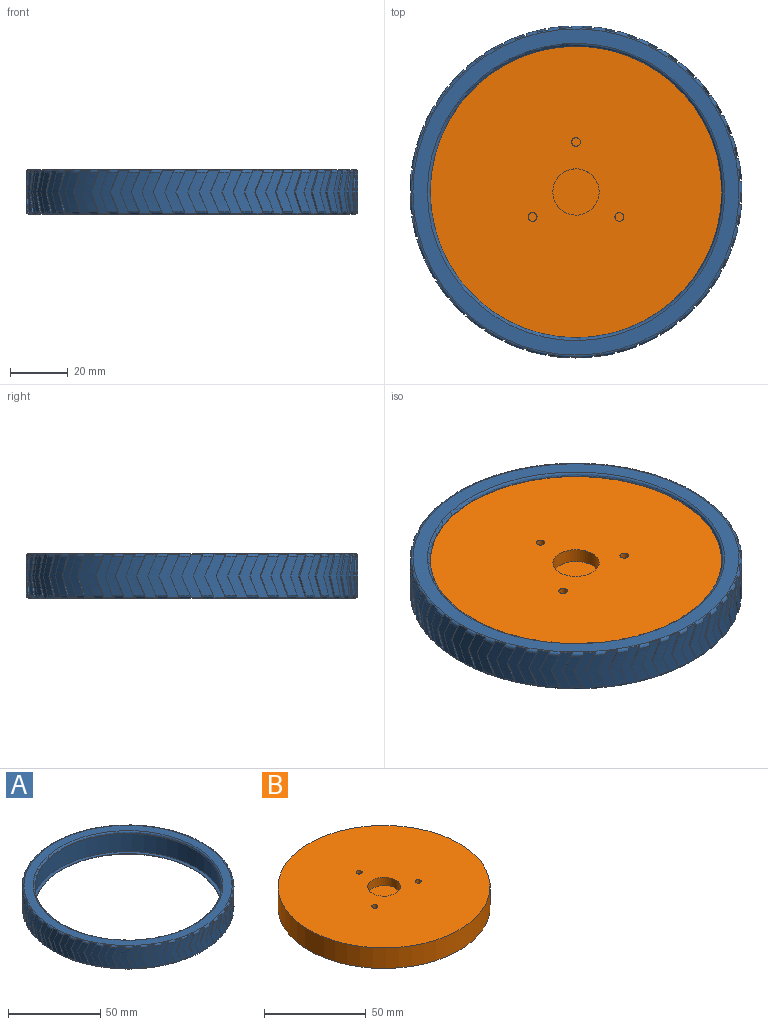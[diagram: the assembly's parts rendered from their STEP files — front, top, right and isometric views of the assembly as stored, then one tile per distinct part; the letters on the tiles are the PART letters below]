
ASSEMBLY  parts=2 mates=1
PART A: 280 faces, bbox 124.3x124.3x15.4 mm
  f0: cylinder r=57.4mm len=13.35mm, axis (0,0,1), area 53.5mm2, adj f45,f46,f272,f273,f275,f276
  f1: cylinder r=57.4mm len=13.35mm, axis (0,0,1), area 53.5mm2, adj f45,f46,f60,f61,f277,f278
  f2: cylinder r=57.4mm len=13.35mm, axis (0,0,1), area 53.5mm2, adj f45,f46,f267,f268,f270,f271
  f3: cylinder r=57.4mm len=13.35mm, axis (0,0,1), area 53.5mm2, adj f45,f46,f262,f263,f265,f266
  f4: cylinder r=57.4mm len=13.35mm, axis (0,0,1), area 53.5mm2, adj f45,f46,f257,f258,f260,f261
  f5: cylinder r=57.4mm len=13.35mm, axis (0,0,1), area 53.5mm2, adj f45,f46,f252,f253,f255,f256
  f6: cylinder r=57.4mm len=13.35mm, axis (0,0,1), area 53.5mm2, adj f45,f46,f247,f248,f250,f251
  f7: cylinder r=57.4mm len=13.35mm, axis (0,0,1), area 53.5mm2, adj f45,f46,f242,f243,f245,f246
  f8: cylinder r=57.4mm len=13.35mm, axis (0,0,1), area 53.5mm2, adj f45,f46,f237,f238,f240,f241
  f9: cylinder r=57.4mm len=13.35mm, axis (0,0,1), area 53.5mm2, adj f45,f46,f232,f233,f235,f236
  f10: cylinder r=57.4mm len=13.35mm, axis (0,0,1), area 53.5mm2, adj f45,f46,f227,f228,f230,f231
  f11: cylinder r=57.4mm len=13.35mm, axis (0,0,1), area 53.5mm2, adj f45,f46,f222,f223,f225,f226
  f12: cylinder r=57.4mm len=13.35mm, axis (0,0,1), area 53.5mm2, adj f45,f46,f217,f218,f220,f221
  f13: cylinder r=57.4mm len=13.35mm, axis (0,0,1), area 53.5mm2, adj f45,f46,f212,f213,f215,f216
  f14: cylinder r=57.4mm len=13.35mm, axis (0,0,1), area 53.5mm2, adj f45,f46,f207,f208,f210,f211
  f15: cylinder r=57.4mm len=13.35mm, axis (0,0,1), area 53.5mm2, adj f45,f46,f202,f203,f205,f206
  f16: cylinder r=57.4mm len=13.35mm, axis (0,0,1), area 53.5mm2, adj f45,f46,f197,f198,f200,f201
  f17: cylinder r=57.4mm len=13.35mm, axis (0,0,1), area 53.5mm2, adj f45,f46,f192,f193,f195,f196
  f18: cylinder r=57.4mm len=13.35mm, axis (0,0,1), area 53.5mm2, adj f45,f46,f187,f188,f190,f191
  f19: cylinder r=57.4mm len=13.35mm, axis (0,0,1), area 53.5mm2, adj f45,f46,f182,f183,f185,f186
  f20: cylinder r=57.4mm len=13.35mm, axis (0,0,1), area 53.5mm2, adj f45,f46,f177,f178,f180,f181
  f21: cylinder r=57.4mm len=13.35mm, axis (0,0,1), area 53.5mm2, adj f45,f46,f172,f173,f175,f176
  f22: cylinder r=57.4mm len=13.35mm, axis (0,0,1), area 53.5mm2, adj f45,f46,f167,f168,f170,f171
  f23: cylinder r=57.4mm len=13.35mm, axis (0,0,1), area 53.5mm2, adj f45,f46,f162,f163,f165,f166
  f24: cylinder r=57.4mm len=13.35mm, axis (0,0,1), area 53.5mm2, adj f45,f46,f157,f158,f160,f161
  f25: cylinder r=57.4mm len=13.35mm, axis (0,0,1), area 53.5mm2, adj f45,f46,f152,f153,f155,f156
  f26: cylinder r=57.4mm len=13.35mm, axis (0,0,1), area 53.5mm2, adj f45,f46,f147,f148,f150,f151
  f27: cylinder r=57.4mm len=13.35mm, axis (0,0,1), area 53.5mm2, adj f45,f46,f142,f143,f145,f146
  f28: cylinder r=57.4mm len=13.35mm, axis (0,0,1), area 53.5mm2, adj f45,f46,f137,f138,f140,f141
  f29: cylinder r=57.4mm len=13.35mm, axis (0,0,1), area 53.5mm2, adj f45,f46,f132,f133,f135,f136
  f30: cylinder r=57.4mm len=13.35mm, axis (0,0,1), area 53.5mm2, adj f45,f46,f127,f128,f130,f131
  f31: cylinder r=57.4mm len=13.35mm, axis (0,0,1), area 53.5mm2, adj f45,f46,f122,f123,f125,f126
  f32: cylinder r=57.4mm len=13.35mm, axis (0,0,1), area 53.5mm2, adj f45,f46,f57,f58,f120,f121
  f33: cylinder r=57.4mm len=13.35mm, axis (0,0,1), area 53.5mm2, adj f45,f46,f112,f113,f115,f116
  f34: cylinder r=57.4mm len=13.35mm, axis (0,0,1), area 53.5mm2, adj f45,f46,f55,f56,f117,f118
  f35: cylinder r=57.4mm len=13.35mm, axis (0,0,1), area 53.5mm2, adj f45,f46,f107,f108,f110,f111
  f36: cylinder r=57.4mm len=13.35mm, axis (0,0,1), area 53.5mm2, adj f45,f46,f102,f103,f105,f106
  f37: cylinder r=57.4mm len=13.35mm, axis (0,0,1), area 53.5mm2, adj f45,f46,f97,f98,f100,f101
  f38: cylinder r=57.4mm len=13.35mm, axis (0,0,1), area 53.5mm2, adj f45,f46,f92,f93,f95,f96
  f39: cylinder r=57.4mm len=13.35mm, axis (0,0,1), area 53.5mm2, adj f45,f46,f87,f88,f90,f91
  f40: cylinder r=57.4mm len=13.35mm, axis (0,0,1), area 53.5mm2, adj f45,f46,f82,f83,f85,f86
  f41: cylinder r=57.4mm len=13.35mm, axis (0,0,1), area 53.5mm2, adj f45,f46,f77,f78,f80,f81
  f42: cylinder r=57.4mm len=13.35mm, axis (0,0,1), area 53.5mm2, adj f45,f46,f72,f73,f75,f76
  f43: cylinder r=57.4mm len=13.35mm, axis (0,0,1), area 53.5mm2, adj f45,f46,f67,f68,f70,f71
  f44: cylinder r=57.4mm len=13.35mm, axis (0,0,1), area 53.5mm2, adj f45,f46,f62,f63,f65,f66
  f45: torus R=56.4mm, axis (0,0,-1), area 356.7mm2, adj f0,f1,f2,f3,f4,f5,f6,f7
  f46: torus R=56.4mm, axis (0,0,-1), area 356.7mm2, adj f0,f1,f2,f3,f4,f5,f6,f7
  f47: plane 104.8x104.8mm, normal (0,0,1), area 645.9mm2, adj f48,f54
  f48: cylinder r=52.4mm len=104.8mm, axis (0,0,1), area 4197.8mm2, adj f47,f49
  f49: cone r=52.4mm half-angle=73.3deg, axis (0,0,-1), area 674.4mm2, adj f48,f50
  f50: cylinder r=50.4mm len=100.8mm, axis (0,0,1), area 63.3mm2, adj f49,f53
  f51: plane 112.8x112.8mm, normal (0,0,1), area 1693.3mm2, adj f45,f53
  f52: plane 112.8x112.8mm, normal (0,0,-1), area 1699.8mm2, adj f46,f54
  f53: torus R=51.4mm, axis (0,0,-1), area 501mm2, adj f50,f51
  f54: torus R=51.38mm, axis (0,0,-1), area 437.1mm2, adj f47,f52
  f55: plane 7.58x3.24mm, normal (-0.92,0,-0.39), area 4.7mm2, adj f34,f46,f56,f59
  f56: plane 7.58x3.24mm, normal (-0.92,0,0.39), area 4.7mm2, adj f34,f45,f55,f59
  f57: plane 7.58x3.24mm, normal (0.92,0,-0.39), area 3.6mm2, adj f32,f45,f58,f59
  f58: plane 7.58x3.24mm, normal (0.92,0,0.39), area 3.6mm2, adj f32,f46,f57,f59
  f59: plane 15.18x7.24mm, normal (0,-1,0), area 60.7mm2, adj f45,f46,f55,f56,f57,f58
  f60: plane 7.58x3.22mm, normal (0.1,-0.91,-0.39), area 4.7mm2, adj f1,f46,f61,f64
  f61: plane 7.58x3.22mm, normal (0.1,-0.91,0.39), area 4.7mm2, adj f1,f45,f60,f64
  f62: plane 7.58x3.22mm, normal (-0.1,0.91,-0.39), area 3.6mm2, adj f44,f45,f63,f64
  f63: plane 7.58x3.22mm, normal (-0.1,0.91,0.39), area 3.6mm2, adj f44,f46,f62,f64
  f64: plane 15.18x7.2mm, normal (0.99,0.1,0), area 60.7mm2, adj f45,f46,f60,f61,f62,f63
  f65: plane 7.58x3.26mm, normal (-0.03,-0.92,-0.39), area 4.7mm2, adj f44,f46,f66,f69
  f66: plane 7.58x3.26mm, normal (-0.03,-0.92,0.39), area 4.7mm2, adj f44,f45,f65,f69
  f67: plane 7.58x3.25mm, normal (0.03,0.92,-0.39), area 3.6mm2, adj f43,f45,f68,f69
  f68: plane 7.58x3.25mm, normal (0.03,0.92,0.39), area 3.6mm2, adj f43,f46,f67,f69
  f69: plane 15.18x7.24mm, normal (1,-0.03,0), area 60.7mm2, adj f45,f46,f65,f66,f67,f68
  f70: plane 7.58x3.29mm, normal (-0.16,-0.91,-0.39), area 4.7mm2, adj f43,f46,f71,f74
  f71: plane 7.58x3.29mm, normal (-0.16,-0.91,0.39), area 4.7mm2, adj f43,f45,f70,f74
  f72: plane 7.58x3.25mm, normal (0.16,0.91,-0.39), area 3.6mm2, adj f42,f45,f73,f74
  f73: plane 7.58x3.25mm, normal (0.16,0.91,0.39), area 3.6mm2, adj f42,f46,f72,f74
  f74: plane 15.18x7.13mm, normal (0.98,-0.17,0), area 60.7mm2, adj f45,f46,f70,f71,f72,f73
  f75: plane 7.58x3.26mm, normal (-0.28,-0.87,-0.39), area 4.7mm2, adj f42,f46,f76,f79
  f76: plane 7.58x3.26mm, normal (-0.28,-0.87,0.39), area 4.7mm2, adj f42,f45,f75,f79
  f77: plane 7.58x3.19mm, normal (0.28,0.87,-0.39), area 3.6mm2, adj f41,f45,f78,f79
  f78: plane 7.58x3.19mm, normal (0.28,0.87,0.39), area 3.6mm2, adj f41,f46,f77,f79
  f79: plane 15.18x6.89mm, normal (0.95,-0.31,0), area 60.7mm2, adj f45,f46,f75,f76,f77,f78
  f80: plane 7.58x3.17mm, normal (-0.4,-0.83,-0.39), area 4.7mm2, adj f41,f46,f81,f84
  f81: plane 7.58x3.17mm, normal (-0.4,-0.83,0.39), area 4.7mm2, adj f41,f45,f80,f84
  f82: plane 7.58x3.06mm, normal (0.4,0.83,-0.39), area 3.6mm2, adj f40,f45,f83,f84
  f83: plane 7.58x3.06mm, normal (0.4,0.83,0.39), area 3.6mm2, adj f40,f46,f82,f84
  f84: plane 15.18x6.51mm, normal (0.9,-0.44,0), area 60.7mm2, adj f45,f46,f80,f81,f82,f83
  f85: plane 7.58x3.01mm, normal (-0.51,-0.76,-0.39), area 4.7mm2, adj f40,f46,f86,f89
  f86: plane 7.58x3.01mm, normal (-0.51,-0.76,0.39), area 4.7mm2, adj f40,f45,f85,f89
  f87: plane 7.58x2.87mm, normal (0.51,0.76,-0.39), area 3.6mm2, adj f39,f45,f88,f89
  f88: plane 7.58x2.87mm, normal (0.51,0.76,0.39), area 3.6mm2, adj f39,f46,f87,f89
  f89: plane 15.18x6mm, normal (0.83,-0.56,0), area 60.7mm2, adj f45,f46,f85,f86,f87,f88
  f90: plane 7.58x2.8mm, normal (-0.62,-0.68,-0.39), area 4.7mm2, adj f39,f46,f91,f94
  f91: plane 7.58x2.8mm, normal (-0.62,-0.68,0.39), area 4.7mm2, adj f39,f45,f90,f94
  f92: plane 7.58x2.63mm, normal (0.62,0.68,-0.39), area 3.6mm2, adj f38,f45,f93,f94
  f93: plane 7.58x2.63mm, normal (0.62,0.68,0.39), area 3.6mm2, adj f38,f46,f92,f94
  f94: plane 15.18x5.38mm, normal (0.74,-0.67,0), area 60.7mm2, adj f45,f46,f90,f91,f92,f93
  f95: plane 7.58x2.64mm, normal (-0.7,-0.59,-0.39), area 4.7mm2, adj f38,f46,f96,f99
  f96: plane 7.58x2.64mm, normal (-0.7,-0.59,0.39), area 4.7mm2, adj f38,f45,f95,f99
  f97: plane 7.58x2.62mm, normal (0.7,0.59,-0.39), area 3.6mm2, adj f37,f45,f98,f99
  f98: plane 7.58x2.62mm, normal (0.7,0.59,0.39), area 3.6mm2, adj f37,f46,f97,f99
  f99: plane 15.18x5.55mm, normal (0.64,-0.77,0), area 60.7mm2, adj f45,f46,f95,f96,f97,f98
  f100: plane 7.58x2.84mm, normal (-0.78,-0.49,-0.39), area 4.7mm2, adj f37,f46,f101,f104
  f101: plane 7.58x2.84mm, normal (-0.78,-0.49,0.39), area 4.7mm2, adj f37,f45,f100,f104
  f102: plane 7.58x2.83mm, normal (0.78,0.49,-0.39), area 3.6mm2, adj f36,f45,f103,f104
  f103: plane 7.58x2.83mm, normal (0.78,0.49,0.39), area 3.6mm2, adj f36,f46,f102,f104
  f104: plane 15.18x6.14mm, normal (0.53,-0.85,0), area 60.7mm2, adj f45,f46,f100,f101,f102,f103
  f105: plane 7.58x3mm, normal (-0.84,-0.37,-0.39), area 4.7mm2, adj f36,f46,f106,f109
  f106: plane 7.58x3mm, normal (-0.84,-0.37,0.39), area 4.7mm2, adj f36,f45,f105,f109
  f107: plane 7.58x2.99mm, normal (0.84,0.37,-0.39), area 3.6mm2, adj f35,f45,f108,f109
  f108: plane 7.58x2.99mm, normal (0.84,0.37,0.39), area 3.6mm2, adj f35,f46,f107,f109
  f109: plane 15.18x6.61mm, normal (0.41,-0.91,0), area 60.7mm2, adj f45,f46,f105,f106,f107,f108
  f110: plane 7.58x3.12mm, normal (-0.88,-0.25,-0.39), area 4.7mm2, adj f35,f46,f111,f114
  f111: plane 7.58x3.12mm, normal (-0.88,-0.25,0.39), area 4.7mm2, adj f35,f45,f110,f114
  f112: plane 7.58x3.12mm, normal (0.88,0.25,-0.39), area 3.6mm2, adj f33,f45,f113,f114
  f113: plane 7.58x3.12mm, normal (0.88,0.25,0.39), area 3.6mm2, adj f33,f46,f112,f114
  f114: plane 15.18x6.96mm, normal (0.28,-0.96,0), area 60.7mm2, adj f45,f46,f110,f111,f112,f113
  f115: plane 7.58x3.21mm, normal (-0.91,-0.13,-0.39), area 4.7mm2, adj f33,f46,f116,f119
  f116: plane 7.58x3.21mm, normal (-0.91,-0.13,0.39), area 4.7mm2, adj f33,f45,f115,f119
  f117: plane 7.58x3.21mm, normal (0.91,0.13,-0.39), area 3.6mm2, adj f34,f45,f118,f119
  f118: plane 7.58x3.21mm, normal (0.91,0.13,0.39), area 3.6mm2, adj f34,f46,f117,f119
  f119: plane 15.18x7.17mm, normal (0.14,-0.99,0), area 60.7mm2, adj f45,f46,f115,f116,f117,f118
  f120: plane 7.58x3.29mm, normal (-0.91,0.13,-0.39), area 4.7mm2, adj f32,f46,f121,f124
  f121: plane 7.58x3.29mm, normal (-0.91,0.13,0.39), area 4.7mm2, adj f32,f45,f120,f124
  f122: plane 7.58x3.26mm, normal (0.91,-0.13,-0.39), area 3.6mm2, adj f31,f45,f123,f124
  f123: plane 7.58x3.26mm, normal (0.91,-0.13,0.39), area 3.6mm2, adj f31,f46,f122,f124
  f124: plane 15.18x7.17mm, normal (-0.14,-0.99,0), area 60.7mm2, adj f45,f46,f120,f121,f122,f123
  f125: plane 7.58x3.27mm, normal (-0.88,0.25,-0.39), area 4.7mm2, adj f31,f46,f126,f129
  f126: plane 7.58x3.27mm, normal (-0.88,0.25,0.39), area 4.7mm2, adj f31,f45,f125,f129
  f127: plane 7.58x3.21mm, normal (0.88,-0.25,-0.39), area 3.6mm2, adj f30,f45,f128,f129
  f128: plane 7.58x3.21mm, normal (0.88,-0.25,0.39), area 3.6mm2, adj f30,f46,f127,f129
  f129: plane 15.18x6.96mm, normal (-0.28,-0.96,0), area 60.7mm2, adj f45,f46,f125,f126,f127,f128
  f130: plane 7.58x3.2mm, normal (-0.84,0.37,-0.39), area 4.7mm2, adj f30,f46,f131,f134
  f131: plane 7.58x3.2mm, normal (-0.84,0.37,0.39), area 4.7mm2, adj f30,f45,f130,f134
  f132: plane 7.58x3.1mm, normal (0.84,-0.37,-0.39), area 3.6mm2, adj f29,f45,f133,f134
  f133: plane 7.58x3.1mm, normal (0.84,-0.37,0.39), area 3.6mm2, adj f29,f46,f132,f134
  f134: plane 15.18x6.61mm, normal (-0.41,-0.91,0), area 60.7mm2, adj f45,f46,f130,f131,f132,f133
  f135: plane 7.58x3.06mm, normal (-0.78,0.49,-0.39), area 4.7mm2, adj f29,f46,f136,f139
  f136: plane 7.58x3.06mm, normal (-0.78,0.49,0.39), area 4.7mm2, adj f29,f45,f135,f139
  f137: plane 7.58x2.93mm, normal (0.78,-0.49,-0.39), area 3.6mm2, adj f28,f45,f138,f139
  f138: plane 7.58x2.93mm, normal (0.78,-0.49,0.39), area 3.6mm2, adj f28,f46,f137,f139
  f139: plane 15.18x6.14mm, normal (-0.53,-0.85,0), area 60.7mm2, adj f45,f46,f135,f136,f137,f138
  f140: plane 7.58x2.86mm, normal (-0.7,0.59,-0.39), area 4.7mm2, adj f28,f46,f141,f144
  f141: plane 7.58x2.86mm, normal (-0.7,0.59,0.39), area 4.7mm2, adj f28,f45,f140,f144
  f142: plane 7.58x2.7mm, normal (0.7,-0.59,-0.39), area 3.6mm2, adj f27,f45,f143,f144
  f143: plane 7.58x2.7mm, normal (0.7,-0.59,0.39), area 3.6mm2, adj f27,f46,f142,f144
  f144: plane 15.18x5.55mm, normal (-0.64,-0.77,0), area 60.7mm2, adj f45,f46,f140,f141,f142,f143
  f145: plane 7.58x2.6mm, normal (-0.62,0.68,-0.39), area 4.7mm2, adj f27,f46,f146,f149
  f146: plane 7.58x2.6mm, normal (-0.62,0.68,0.39), area 4.7mm2, adj f27,f45,f145,f149
  f147: plane 7.58x2.56mm, normal (0.62,-0.68,-0.39), area 3.6mm2, adj f26,f45,f148,f149
  f148: plane 7.58x2.56mm, normal (0.62,-0.68,0.39), area 3.6mm2, adj f26,f46,f147,f149
  f149: plane 15.18x5.38mm, normal (-0.74,-0.67,0), area 60.7mm2, adj f45,f46,f145,f146,f147,f148
  f150: plane 7.58x2.79mm, normal (-0.51,0.76,-0.39), area 4.7mm2, adj f26,f46,f151,f154
  f151: plane 7.58x2.79mm, normal (-0.51,0.76,0.39), area 4.7mm2, adj f26,f45,f150,f154
  f152: plane 7.58x2.78mm, normal (0.51,-0.76,-0.39), area 3.6mm2, adj f25,f45,f153,f154
  f153: plane 7.58x2.78mm, normal (0.51,-0.76,0.39), area 3.6mm2, adj f25,f46,f152,f154
  f154: plane 15.18x6mm, normal (-0.83,-0.56,0), area 60.7mm2, adj f45,f46,f150,f151,f152,f153
  f155: plane 7.58x2.96mm, normal (-0.4,0.83,-0.39), area 4.7mm2, adj f25,f46,f156,f159
  f156: plane 7.58x2.96mm, normal (-0.4,0.83,0.39), area 4.7mm2, adj f25,f45,f155,f159
  f157: plane 7.58x2.96mm, normal (0.4,-0.83,-0.39), area 3.6mm2, adj f24,f45,f158,f159
  f158: plane 7.58x2.96mm, normal (0.4,-0.83,0.39), area 3.6mm2, adj f24,f46,f157,f159
  f159: plane 15.18x6.51mm, normal (-0.9,-0.44,0), area 60.7mm2, adj f45,f46,f155,f156,f157,f158
  f160: plane 7.58x3.09mm, normal (-0.28,0.87,-0.39), area 4.7mm2, adj f24,f46,f161,f164
  f161: plane 7.58x3.09mm, normal (-0.28,0.87,0.39), area 4.7mm2, adj f24,f45,f160,f164
  f162: plane 7.58x3.09mm, normal (0.28,-0.87,-0.39), area 3.6mm2, adj f23,f45,f163,f164
  f163: plane 7.58x3.09mm, normal (0.28,-0.87,0.39), area 3.6mm2, adj f23,f46,f162,f164
  f164: plane 15.18x6.89mm, normal (-0.95,-0.31,0), area 60.7mm2, adj f45,f46,f160,f161,f162,f163
  f165: plane 7.58x3.19mm, normal (-0.16,0.91,-0.39), area 4.7mm2, adj f23,f46,f166,f169
  f166: plane 7.58x3.19mm, normal (-0.16,0.91,0.39), area 4.7mm2, adj f23,f45,f165,f169
  f167: plane 7.58x3.19mm, normal (0.16,-0.91,-0.39), area 3.6mm2, adj f22,f45,f168,f169
  f168: plane 7.58x3.19mm, normal (0.16,-0.91,0.39), area 3.6mm2, adj f22,f46,f167,f169
  f169: plane 15.18x7.13mm, normal (-0.98,-0.17,0), area 60.7mm2, adj f45,f46,f165,f166,f167,f168
  f170: plane 7.58x3.24mm, normal (-0.03,0.92,-0.39), area 4.7mm2, adj f22,f46,f171,f174
  f171: plane 7.58x3.24mm, normal (-0.03,0.92,0.39), area 4.7mm2, adj f22,f45,f170,f174
  f172: plane 7.58x3.24mm, normal (0.03,-0.92,-0.39), area 3.6mm2, adj f21,f45,f173,f174
  f173: plane 7.58x3.24mm, normal (0.03,-0.92,0.39), area 3.6mm2, adj f21,f46,f172,f174
  f174: plane 15.18x7.24mm, normal (-1,-0.03,0), area 60.7mm2, adj f45,f46,f170,f171,f172,f173
  f175: plane 7.58x3.28mm, normal (0.1,0.91,-0.39), area 4.7mm2, adj f21,f46,f176,f179
  f176: plane 7.58x3.28mm, normal (0.1,0.91,0.39), area 4.7mm2, adj f21,f45,f175,f179
  f177: plane 7.58x3.26mm, normal (-0.1,-0.91,-0.39), area 3.6mm2, adj f20,f45,f178,f179
  f178: plane 7.58x3.26mm, normal (-0.1,-0.91,0.39), area 3.6mm2, adj f20,f46,f177,f179
  f179: plane 15.18x7.2mm, normal (-0.99,0.1,0), area 60.7mm2, adj f45,f46,f175,f176,f177,f178
  f180: plane 7.58x3.28mm, normal (0.22,0.89,-0.39), area 4.7mm2, adj f20,f46,f181,f184
  f181: plane 7.58x3.28mm, normal (0.22,0.89,0.39), area 4.7mm2, adj f20,f45,f180,f184
  f182: plane 7.58x3.23mm, normal (-0.22,-0.89,-0.39), area 3.6mm2, adj f19,f45,f183,f184
  f183: plane 7.58x3.23mm, normal (-0.22,-0.89,0.39), area 3.6mm2, adj f19,f46,f182,f184
  f184: plane 15.18x7.02mm, normal (-0.97,0.24,0), area 60.7mm2, adj f45,f46,f180,f181,f182,f183
  f185: plane 7.58x3.22mm, normal (0.34,0.85,-0.39), area 4.7mm2, adj f19,f46,f186,f189
  f186: plane 7.58x3.22mm, normal (0.34,0.85,0.39), area 4.7mm2, adj f19,f45,f185,f189
  f187: plane 7.58x3.13mm, normal (-0.34,-0.85,-0.39), area 3.6mm2, adj f18,f45,f188,f189
  f188: plane 7.58x3.13mm, normal (-0.34,-0.85,0.39), area 3.6mm2, adj f18,f46,f187,f189
  f189: plane 15.18x6.71mm, normal (-0.93,0.37,0), area 60.7mm2, adj f45,f46,f185,f186,f187,f188
  f190: plane 7.58x3.1mm, normal (0.46,0.8,-0.39), area 4.7mm2, adj f18,f46,f191,f194
  f191: plane 7.58x3.1mm, normal (0.46,0.8,0.39), area 4.7mm2, adj f18,f45,f190,f194
  f192: plane 7.58x2.97mm, normal (-0.46,-0.8,-0.39), area 3.6mm2, adj f17,f45,f193,f194
  f193: plane 7.58x2.97mm, normal (-0.46,-0.8,0.39), area 3.6mm2, adj f17,f46,f192,f194
  f194: plane 15.18x6.27mm, normal (-0.87,0.5,0), area 60.7mm2, adj f45,f46,f190,f191,f192,f193
  f195: plane 7.58x2.91mm, normal (0.57,0.72,-0.39), area 4.7mm2, adj f17,f46,f196,f199
  f196: plane 7.58x2.91mm, normal (0.57,0.72,0.39), area 4.7mm2, adj f17,f45,f195,f199
  f197: plane 7.58x2.76mm, normal (-0.57,-0.72,-0.39), area 3.6mm2, adj f16,f45,f198,f199
  f198: plane 7.58x2.76mm, normal (-0.57,-0.72,0.39), area 3.6mm2, adj f16,f46,f197,f199
  f199: plane 15.18x5.71mm, normal (-0.79,0.62,0), area 60.7mm2, adj f45,f46,f195,f196,f197,f198
  f200: plane 7.58x2.67mm, normal (0.66,0.64,-0.39), area 4.7mm2, adj f16,f46,f201,f204
  f201: plane 7.58x2.67mm, normal (0.66,0.64,0.39), area 4.7mm2, adj f16,f45,f200,f204
  f202: plane 7.58x2.5mm, normal (-0.66,-0.64,-0.39), area 3.6mm2, adj f15,f45,f203,f204
  f203: plane 7.58x2.5mm, normal (-0.66,-0.64,0.39), area 3.6mm2, adj f15,f46,f202,f204
  f204: plane 15.18x5.21mm, normal (-0.69,0.72,0), area 60.7mm2, adj f45,f46,f200,f201,f202,f203
  f205: plane 7.58x2.74mm, normal (0.74,0.54,-0.39), area 4.7mm2, adj f15,f46,f206,f209
  f206: plane 7.58x2.74mm, normal (0.74,0.54,0.39), area 4.7mm2, adj f15,f45,f205,f209
  f207: plane 7.58x2.73mm, normal (-0.74,-0.54,-0.39), area 3.6mm2, adj f14,f45,f208,f209
  f208: plane 7.58x2.73mm, normal (-0.74,-0.54,0.39), area 3.6mm2, adj f14,f46,f207,f209
  f209: plane 15.18x5.86mm, normal (-0.59,0.81,0), area 60.7mm2, adj f45,f46,f205,f206,f207,f208
  f210: plane 7.58x2.92mm, normal (0.81,0.43,-0.39), area 4.7mm2, adj f14,f46,f211,f214
  f211: plane 7.58x2.92mm, normal (0.81,0.43,0.39), area 4.7mm2, adj f14,f45,f210,f214
  f212: plane 7.58x2.92mm, normal (-0.81,-0.43,-0.39), area 3.6mm2, adj f13,f45,f213,f214
  f213: plane 7.58x2.92mm, normal (-0.81,-0.43,0.39), area 3.6mm2, adj f13,f46,f212,f214
  f214: plane 15.18x6.39mm, normal (-0.47,0.88,0), area 60.7mm2, adj f45,f46,f210,f211,f212,f213
  f215: plane 7.58x3.06mm, normal (0.86,0.31,-0.39), area 4.7mm2, adj f13,f46,f216,f219
  f216: plane 7.58x3.06mm, normal (0.86,0.31,0.39), area 4.7mm2, adj f13,f45,f215,f219
  f217: plane 7.58x3.06mm, normal (-0.86,-0.31,-0.39), area 3.6mm2, adj f12,f45,f218,f219
  f218: plane 7.58x3.06mm, normal (-0.86,-0.31,0.39), area 3.6mm2, adj f12,f46,f217,f219
  f219: plane 15.18x6.8mm, normal (-0.34,0.94,0), area 60.7mm2, adj f45,f46,f215,f216,f217,f218
  f220: plane 7.58x3.17mm, normal (0.9,0.19,-0.39), area 4.7mm2, adj f12,f46,f221,f224
  f221: plane 7.58x3.17mm, normal (0.9,0.19,0.39), area 4.7mm2, adj f12,f45,f220,f224
  f222: plane 7.58x3.17mm, normal (-0.9,-0.19,-0.39), area 3.6mm2, adj f11,f45,f223,f224
  f223: plane 7.58x3.17mm, normal (-0.9,-0.19,0.39), area 3.6mm2, adj f11,f46,f222,f224
  f224: plane 15.18x7.08mm, normal (-0.21,0.98,0), area 60.7mm2, adj f45,f46,f220,f221,f222,f223
  f225: plane 7.58x3.23mm, normal (0.92,0.06,-0.39), area 4.7mm2, adj f11,f46,f226,f229
  f226: plane 7.58x3.23mm, normal (0.92,0.06,0.39), area 4.7mm2, adj f11,f45,f225,f229
  f227: plane 7.58x3.23mm, normal (-0.92,-0.06,-0.39), area 3.6mm2, adj f10,f45,f228,f229
  f228: plane 7.58x3.23mm, normal (-0.92,-0.06,0.39), area 3.6mm2, adj f10,f46,f227,f229
  f229: plane 15.18x7.22mm, normal (-0.07,1,0), area 60.7mm2, adj f45,f46,f225,f226,f227,f228
  f230: plane 7.58x3.27mm, normal (0.92,-0.06,-0.39), area 4.7mm2, adj f10,f46,f231,f234
  f231: plane 7.58x3.27mm, normal (0.92,-0.06,0.39), area 4.7mm2, adj f10,f45,f230,f234
  f232: plane 7.58x3.26mm, normal (-0.92,0.06,-0.39), area 3.6mm2, adj f9,f45,f233,f234
  f233: plane 7.58x3.26mm, normal (-0.92,0.06,0.39), area 3.6mm2, adj f9,f46,f232,f234
  f234: plane 15.18x7.22mm, normal (0.07,1,0), area 60.7mm2, adj f45,f46,f230,f231,f232,f233
  f235: plane 7.58x3.29mm, normal (0.9,-0.19,-0.39), area 4.7mm2, adj f9,f46,f236,f239
  f236: plane 7.58x3.29mm, normal (0.9,-0.19,0.39), area 4.7mm2, adj f9,f45,f235,f239
  f237: plane 7.58x3.24mm, normal (-0.9,0.19,-0.39), area 3.6mm2, adj f8,f45,f238,f239
  f238: plane 7.58x3.24mm, normal (-0.9,0.19,0.39), area 3.6mm2, adj f8,f46,f237,f239
  f239: plane 15.18x7.08mm, normal (0.21,0.98,0), area 60.7mm2, adj f45,f46,f235,f236,f237,f238
  f240: plane 7.58x3.24mm, normal (0.86,-0.31,-0.39), area 4.7mm2, adj f8,f46,f241,f244
  f241: plane 7.58x3.24mm, normal (0.86,-0.31,0.39), area 4.7mm2, adj f8,f45,f240,f244
  f242: plane 7.58x3.16mm, normal (-0.86,0.31,-0.39), area 3.6mm2, adj f7,f45,f243,f244
  f243: plane 7.58x3.16mm, normal (-0.86,0.31,0.39), area 3.6mm2, adj f7,f46,f242,f244
  f244: plane 15.18x6.8mm, normal (0.34,0.94,0), area 60.7mm2, adj f45,f46,f240,f241,f242,f243
  f245: plane 7.58x3.13mm, normal (0.81,-0.43,-0.39), area 4.7mm2, adj f7,f46,f246,f249
  f246: plane 7.58x3.13mm, normal (0.81,-0.43,0.39), area 4.7mm2, adj f7,f45,f245,f249
  f247: plane 7.58x3.02mm, normal (-0.81,0.43,-0.39), area 3.6mm2, adj f6,f45,f248,f249
  f248: plane 7.58x3.02mm, normal (-0.81,0.43,0.39), area 3.6mm2, adj f6,f46,f247,f249
  f249: plane 15.18x6.39mm, normal (0.47,0.88,0), area 60.7mm2, adj f45,f46,f245,f246,f247,f248
  f250: plane 7.58x2.96mm, normal (0.74,-0.54,-0.39), area 4.7mm2, adj f6,f46,f251,f254
  f251: plane 7.58x2.96mm, normal (0.74,-0.54,0.39), area 4.7mm2, adj f6,f45,f250,f254
  f252: plane 7.58x2.82mm, normal (-0.74,0.54,-0.39), area 3.6mm2, adj f5,f45,f253,f254
  f253: plane 7.58x2.82mm, normal (-0.74,0.54,0.39), area 3.6mm2, adj f5,f46,f252,f254
  f254: plane 15.18x5.86mm, normal (0.59,0.81,0), area 60.7mm2, adj f45,f46,f250,f251,f252,f253
  f255: plane 7.58x2.73mm, normal (0.66,-0.64,-0.39), area 4.7mm2, adj f5,f46,f256,f259
  f256: plane 7.58x2.73mm, normal (0.66,-0.64,0.39), area 4.7mm2, adj f5,f45,f255,f259
  f257: plane 7.58x2.56mm, normal (-0.66,0.64,-0.39), area 3.6mm2, adj f4,f45,f258,f259
  f258: plane 7.58x2.56mm, normal (-0.66,0.64,0.39), area 3.6mm2, adj f4,f46,f257,f259
  f259: plane 15.18x5.21mm, normal (0.69,0.72,0), area 60.7mm2, adj f45,f46,f255,f256,f257,f258
  f260: plane 7.58x2.69mm, normal (0.57,-0.72,-0.39), area 4.7mm2, adj f4,f46,f261,f264
  f261: plane 7.58x2.69mm, normal (0.57,-0.72,0.39), area 4.7mm2, adj f4,f45,f260,f264
  f262: plane 7.58x2.68mm, normal (-0.57,0.72,-0.39), area 3.6mm2, adj f3,f45,f263,f264
  f263: plane 7.58x2.68mm, normal (-0.57,0.72,0.39), area 3.6mm2, adj f3,f46,f262,f264
  f264: plane 15.18x5.71mm, normal (0.79,0.62,0), area 60.7mm2, adj f45,f46,f260,f261,f262,f263
  f265: plane 7.58x2.88mm, normal (0.46,-0.8,-0.39), area 4.7mm2, adj f3,f46,f266,f269
  f266: plane 7.58x2.88mm, normal (0.46,-0.8,0.39), area 4.7mm2, adj f3,f45,f265,f269
  f267: plane 7.58x2.87mm, normal (-0.46,0.8,-0.39), area 3.6mm2, adj f2,f45,f268,f269
  f268: plane 7.58x2.87mm, normal (-0.46,0.8,0.39), area 3.6mm2, adj f2,f46,f267,f269
  f269: plane 15.18x6.27mm, normal (0.87,0.5,0), area 60.7mm2, adj f45,f46,f265,f266,f267,f268
  f270: plane 7.58x3.03mm, normal (0.34,-0.85,-0.39), area 4.7mm2, adj f2,f46,f271,f274
  f271: plane 7.58x3.03mm, normal (0.34,-0.85,0.39), area 4.7mm2, adj f2,f45,f270,f274
  f272: plane 7.58x3.03mm, normal (-0.34,0.85,-0.39), area 3.6mm2, adj f0,f45,f273,f274
  f273: plane 7.58x3.03mm, normal (-0.34,0.85,0.39), area 3.6mm2, adj f0,f46,f272,f274
  f274: plane 15.18x6.71mm, normal (0.93,0.37,0), area 60.7mm2, adj f45,f46,f270,f271,f272,f273
  f275: plane 7.58x3.15mm, normal (0.22,-0.89,-0.39), area 4.7mm2, adj f0,f46,f276,f279
  f276: plane 7.58x3.15mm, normal (0.22,-0.89,0.39), area 4.7mm2, adj f0,f45,f275,f279
  f277: plane 7.58x3.15mm, normal (-0.22,0.89,-0.39), area 3.6mm2, adj f1,f45,f278,f279
  f278: plane 7.58x3.15mm, normal (-0.22,0.89,0.39), area 3.6mm2, adj f1,f46,f277,f279
  f279: plane 15.18x7.02mm, normal (0.97,0.24,0), area 60.7mm2, adj f45,f46,f275,f276,f277,f278
PART B: 11 faces, bbox 104x104x12.4 mm
  f0: cylinder r=52mm len=104mm, axis (0,0,-1), area 4035.1mm2, adj f1,f2
  f1: plane 104x104mm, normal (0,0,1), area 8272.6mm2, adj f0,f3,f5,f7,f9
  f2: plane 104x104mm, normal (0,0,-1), area 8494.9mm2, adj f0
  f3: cylinder r=1.5mm len=11mm, axis (0,0,1), area 103.7mm2, adj f1,f4
  f4: plane 3x3mm, normal (0,0,1), area 7.1mm2, adj f3
  f5: cylinder r=1.5mm len=11mm, axis (0,0,1), area 103.7mm2, adj f1,f6
  f6: plane 3x3mm, normal (0,0,1), area 7.1mm2, adj f5
  f7: cylinder r=1.5mm len=11mm, axis (0,0,1), area 103.7mm2, adj f1,f8
  f8: plane 3x3mm, normal (0,0,1), area 7.1mm2, adj f7
  f9: cylinder r=8mm len=16mm, axis (0,0,1), area 251.3mm2, adj f1,f10
  f10: plane 16x16mm, normal (0,0,1), area 201.1mm2, adj f9
PLACE A t=(37.17,58.6,-39.01)mm
PLACE B t=(37.17,58.6,-33.56)mm
MATE fastened A.f0 <-> B.f0  axis (0,0,1) through (37.17,58.6,-33.56)mm
